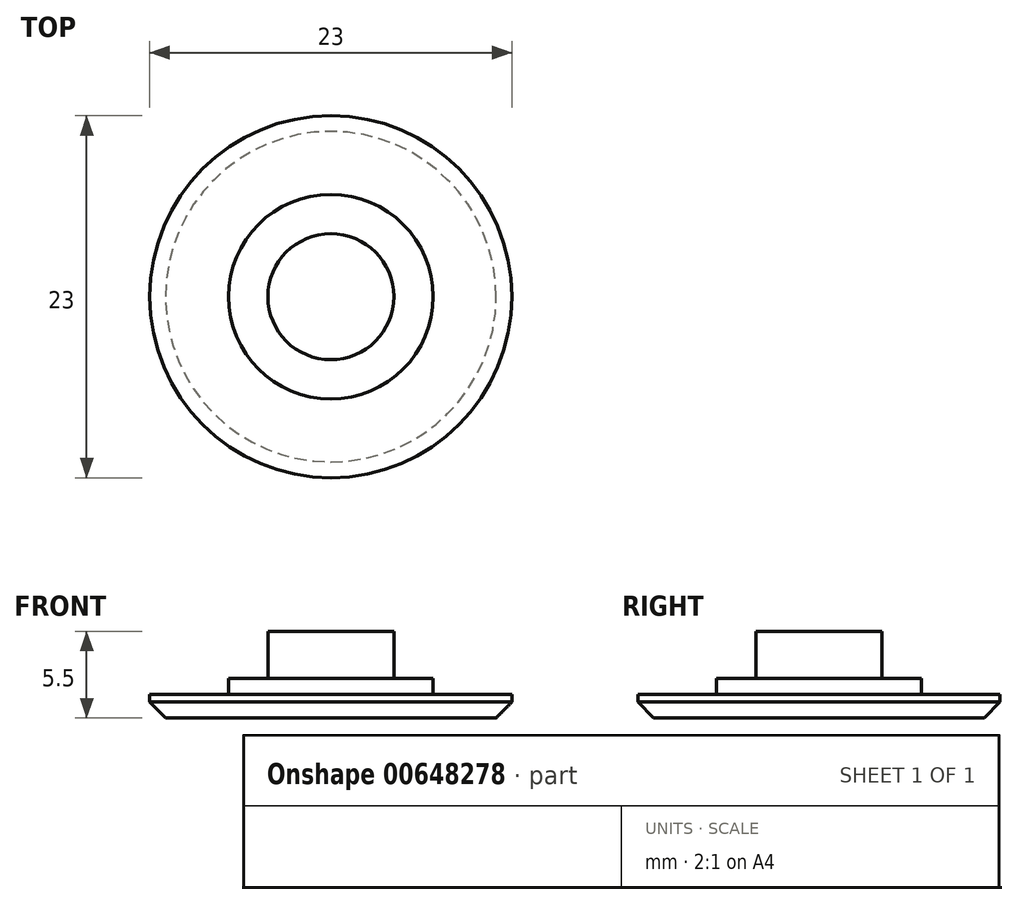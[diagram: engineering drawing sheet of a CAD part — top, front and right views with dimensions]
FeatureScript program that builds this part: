
annotation { "Feature Type Name" : "Feature", "Feature Type Description" : "" }
export const myFeature = defineFeature(function(context is Context, id is Id, definition is map)
    precondition{}
    {
        {
            var Q0;
            Q0=qCreatedBy(makeId("Top.planeOp"),FACE);
            var sketch = newSketch(context, id + "F0", { "sketchPlane" : qUnion([Q0])});
            skCircle(sketch, "E0", {"center": v(0, 0) * mm, "radius": 4 * mm});
            skCircle(sketch, "E1", {"center": v(0, 0) * mm, "radius": 11.5 * mm});
            skCircle(sketch, "E2", {"center": v(0, 0) * mm, "radius": 6.5 * mm});
            skSolve(sketch);
        }
        {
            var Q0;
            Q0=makeQuery(id+"F0.imprint","IMPRINT",FACE,{"disambiguationData":[TD([[makeQuery(id+"F0.imprint","IMPRINT",EDGE,{"derivedFrom":sQuery(id+"F0.wireOp",EDGE,"E1")}),1.0]])]});
            extrude(context, id + "F1", {"entities" : qUnion([Q0]), "depth" : 1.5 * mm, "offsetDistance" : 25.4 * mm});
        }
        {
            var Q0;
            Q0=makeQuery(id+"F0.imprint","IMPRINT",FACE,{"disambiguationData":[TD([[makeQuery(id+"F0.imprint","IMPRINT",EDGE,{"derivedFrom":sQuery(id+"F0.wireOp",EDGE,"E0")}),-1.0]])]});
            extrude(context, id + "F2", {"entities" : qUnion([Q0]), "operationType" : NewBodyOperationType.ADD, "depth" : 2.5 * mm, "offsetDistance" : 25.4 * mm});
        }
        {
            var Q0;
            Q0=makeQuery(id+"F0.imprint","IMPRINT",FACE,{"disambiguationData":[TD([[makeQuery(id+"F0.imprint","IMPRINT",EDGE,{"derivedFrom":sQuery(id+"F0.wireOp",EDGE,"E0")}),1.0]])]});
            extrude(context, id + "F3", {"entities" : qUnion([Q0]), "operationType" : NewBodyOperationType.ADD, "depth" : 5.5 * mm, "offsetDistance" : 25.4 * mm});
        }
        {
            var Q0;
            Q0=makeQuery(id+"F1.opExtrude","CAP_EDGE",EDGE,{"disambiguationData":[OSD([sQuery(id+"F0.wireOp",EDGE,"E1")])],"isStart":true});
            chamfer(context, id + "F4", {"entities" : qUnion([Q0]), "width" : 1 * mm, "tangentPropagation" : true});
        }
    });
